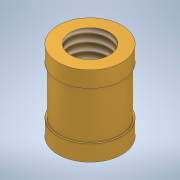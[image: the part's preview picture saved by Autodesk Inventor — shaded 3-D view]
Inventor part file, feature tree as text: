
AUTODESK INVENTOR PART (.ipt)
format: ipt  version: 2020 (Build 240168000, 168)  size: 131,584 bytes
history: native  units: in
note: dims shown in document units (in); Inventor stores cm internally (conversion verified against a paired STEP export)
features: sketch x2, revolve x1, hole x1
ambient origin geometry x8: Origin, YZ Plane, XZ Plane, XY Plane, X Axis, Y Axis, Z Axis, Center Point
bodies: Solid1 (feature_tree)
feature tree (4):
  revolve  "Revolution1"  Angle=90.0deg
  hole  "Hole1"  [1 undecoded]
  sketch  "Sketch1"  dims[d0=0.0787in d1=90.0deg]
  sketch  "Sketch2"  dims[d2=0.0394in d3=0.0039in d4=0.1181in d5=90.0deg d6=0.0039in d7=0.0394in d8=90.0deg d9=0.0787in d10=90.0deg d11=90.0deg d12=0.0968in d13=0.2362in d14=0.1575in d15=0.0787in d16=90.0deg d17=0.3465in d18=0.8108in]
note: 1 required parameter value undecoded (feature->parameter linkage not recoverable at this tier; creation-order binding heuristic only, values carry confidence <= 0.55)
